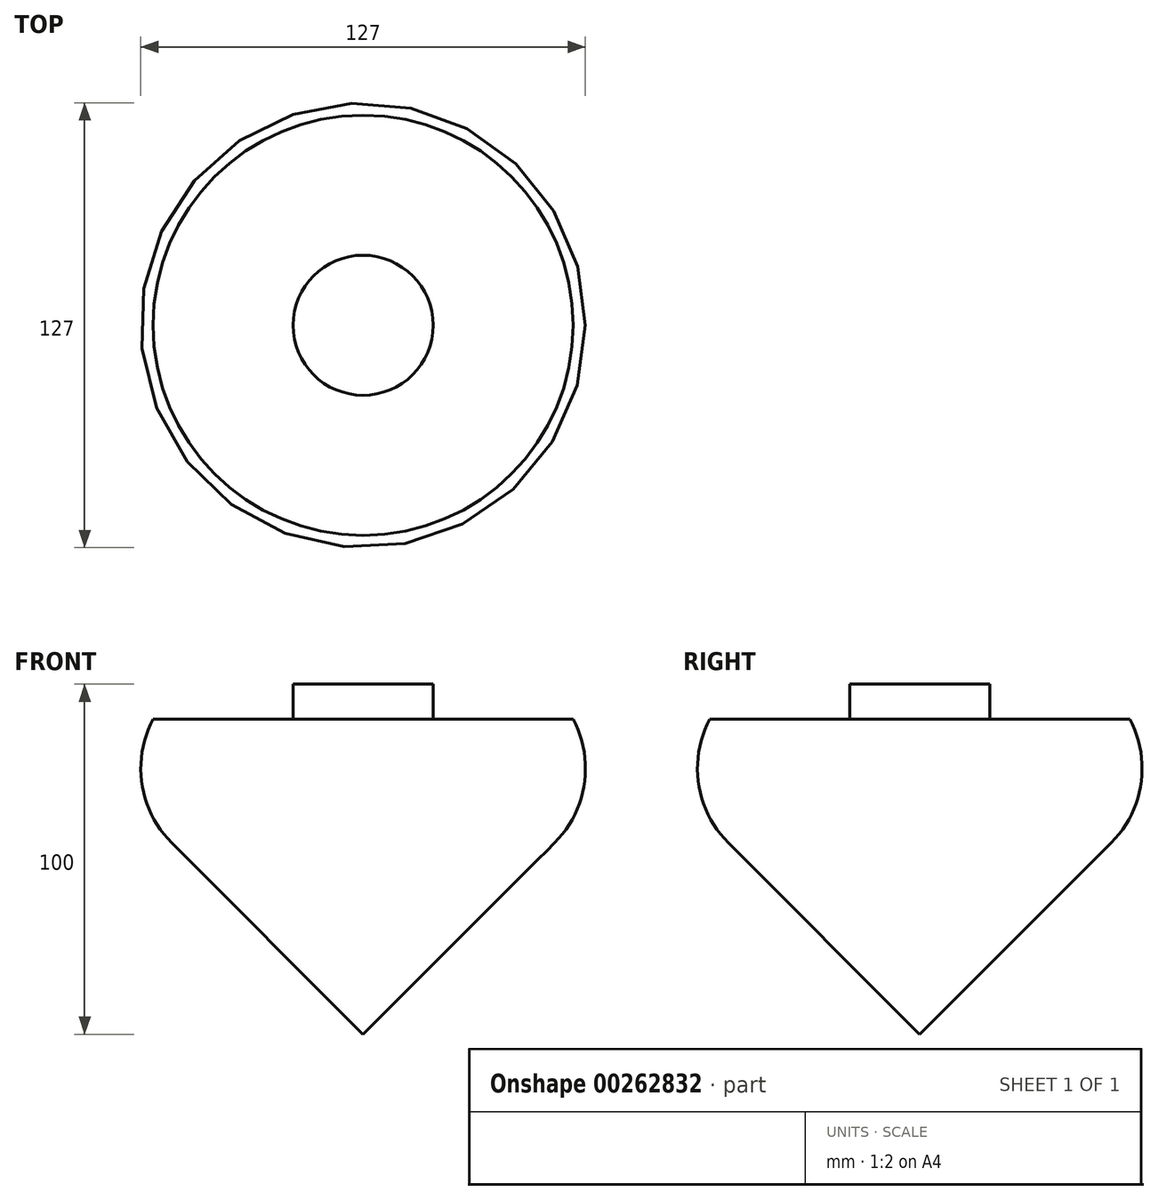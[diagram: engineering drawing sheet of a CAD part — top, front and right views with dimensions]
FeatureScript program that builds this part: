
annotation { "Feature Type Name" : "Feature", "Feature Type Description" : "" }
export const myFeature = defineFeature(function(context is Context, id is Id, definition is map)
    precondition{}
    {
        {
            var Q0;
            Q0=qCreatedBy(makeId("Front.planeOp"),FACE);
            var sketch = newSketch(context, id + "F0", { "sketchPlane" : qUnion([Q0])});
            skLineSegment(sketch, "E0", {"start": v(0, 100) * mm, "end": v(20, 100) * mm});
            skLineSegment(sketch, "E1", {"start": v(20, 100) * mm, "end": v(20, 90) * mm});
            skLineSegment(sketch, "E2", {"start": v(20, 90) * mm, "end": v(60, 90) * mm});
            skLineSegment(sketch, "E3", {"start": v(0, 0) * mm, "end": v(54.72, 54.72) * mm});
            skArc(sketch, "E4", {"start": v(54.72, 54.72) * mm, "mid": v(63.17, 71.49) * mm, "end": v(60, 90) * mm});
            skLineSegment(sketch, "E5", {"start": v(0, 100) * mm, "end": v(0, 0) * mm});
            skSolve(sketch);
        }
        {
            var Q0;
            Q0=makeQuery(id+"F0.imprint","IMPRINT",FACE,{"disambiguationData":[TD([[makeQuery(id+"F0.imprint","IMPRINT",EDGE,{"derivedFrom":sQuery(id+"F0.wireOp",EDGE,"E0")}),-1.0]])]});
            var Q1;
            Q1=sQuery(id+"F0.wireOp",EDGE,"E5");
            revolve(context, id + "F1", {"entities" : qUnion([Q0]), "axis" : qUnion([Q1]), "revolveType" : RevolveType.FULL});
        }
    });
